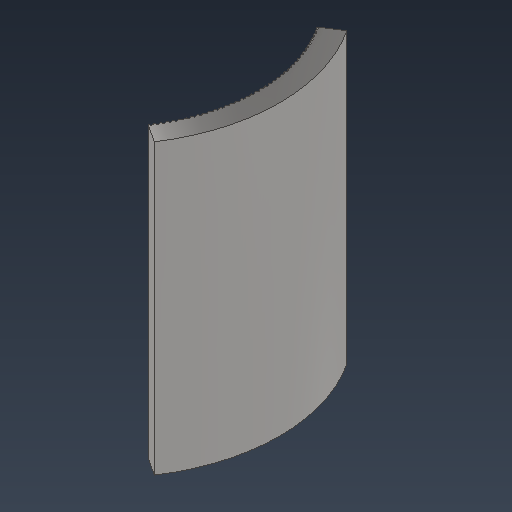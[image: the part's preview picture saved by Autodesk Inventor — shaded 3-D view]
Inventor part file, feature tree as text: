
AUTODESK INVENTOR PART (.ipt)
format: ipt  version: 2021 (Build 250183000, 183)  size: 198,656 bytes
history: native  units: mm
features: extrude x2, sketch x2, pattern_circular x1
ambient origin geometry x8: Origin, YZ Plane, XZ Plane, XY Plane, X Axis, Y Axis, Z Axis, Center Point
bodies: Solid1 (feature_tree)
feature tree (5):
  extrude  "Extrusion1"  Depth=12.133mm
  extrude  "Extrusion2"  Depth=20.0mm
  pattern_circular  "Circular Pattern1"  [2 undecoded]
  sketch  "Sketch1"  dims[d0=12.133mm d2=12.133mm]
  sketch  "Sketch2"  dims[d3=0.0mm d5=2.0mm d6=2.0mm d7=1.5mm d8=20.0mm d9=0.0mm d11=0.1mm d12=10.0mm d13=5.823721mm d14=20.0mm d15=0.145593mm d16=0.0mm d17=0.0mm d18=400.0mm d19=11.657054mm]
note: 2 required parameter values undecoded (feature->parameter linkage not recoverable at this tier; creation-order binding heuristic only, values carry confidence <= 0.55)
